# Revit family: Haworth_Compose_Panel_TileBenching
name_source: partatom
category: Furniture Systems
revit_build: Autodesk Revit 2018 (Build: 20170223_1515(x64)
units: mm (PartAtom-declared; Revit-internal decimal feet)

## family parameters
Always vertical = Yes
Cut with Voids When Loaded = No
OmniClass Number = 23.40.70.14.64.21
OmniClass Title = Systems Furniture
Part Type = Normal
Room Calculation Point = No
Round Connector Dimension = Use Diameter
Shared = No
Work Plane-Based = No

## types (20) — shared parameters
Actual Height = 27"
Assembly Code = E2020500
Description = Haworth - Compose Panel - Accessories Benching - Tile
Manufacturer = Haworth
Max. Height = 27"
Max. Width = 96"
Min. Height = 8"
Min. Width = 18"
Min/Max Height = 19 in., 27 in.
Min/Max Width = 24-96 in. @ 6 in. Increments
Model = VZTI
Panel Depth = 5/8"
Panel Finish = Haworth _ Fabric _ Tellure _ Sky 3A-32
Panel Height = 27"
Revision Number = 5
Size = Verify Final Dim. w/ Haworth
Sustainability Info = http://media.haworth.com
Tackboard = Yes
URL = www.haworth.com
URL - Product = http://www.haworth.com
Warranty = http://www.haworth.com

## per-type parameters (varying)
| type | Actual Width | Height | Panel Width | Width |
| Tackboard 18w 19h | 18" | 19" | 18" | 18" |
| Tackboard 24w 19h | 24" | 19" | 24" | 24" |
| Tackboard 30w 19h | 30" | 19" | 30" | 30" |
| Tackboard 36w 19h | 36" | 19" | 36" | 36" |
| Tackboard 42w 19h | 42" | 19" | 42" | 42" |
| Tackboard 48w 19h | 48" | 19" | 48" | 48" |
| Tackboard 54w 19h | 54" | 19" | 54" | 54" |
| Tackboard 60w 19h | 60" | 19" | 60" | 60" |
| Tackboard 66w 19h | 66" | 19" | 66" | 66" |
| Tackboard 72w 19h | 72" | 19" | 72" | 72" |
| Tackboard 18w 27h | 18" | 27" | 18" | 18" |
| Tackboard 24w 27h | 24" | 27" | 24" | 24" |
| Tackboard 30w 27h | 30" | 27" | 30" | 30" |
| Tackboard 36w 27h | 36" | 27" | 36" | 36" |
| Tackboard 42w 27h | 42" | 27" | 42" | 42" |
| Tackboard 48w 27h | 48" | 27" | 48" | 48" |
| Tackboard 54w 27h | 54" | 27" | 54" | 54" |
| Tackboard 60w 27h | 60" | 27" | 60" | 60" |
| Tackboard 66w 27h | 66" | 27" | 66" | 66" |
| Tackboard 72w 27h | 72" | 27" | 72" | 72" |

## geometry (parser evidence)
native form markers: Sweep x6
no freeform markers — native parametric forms only
